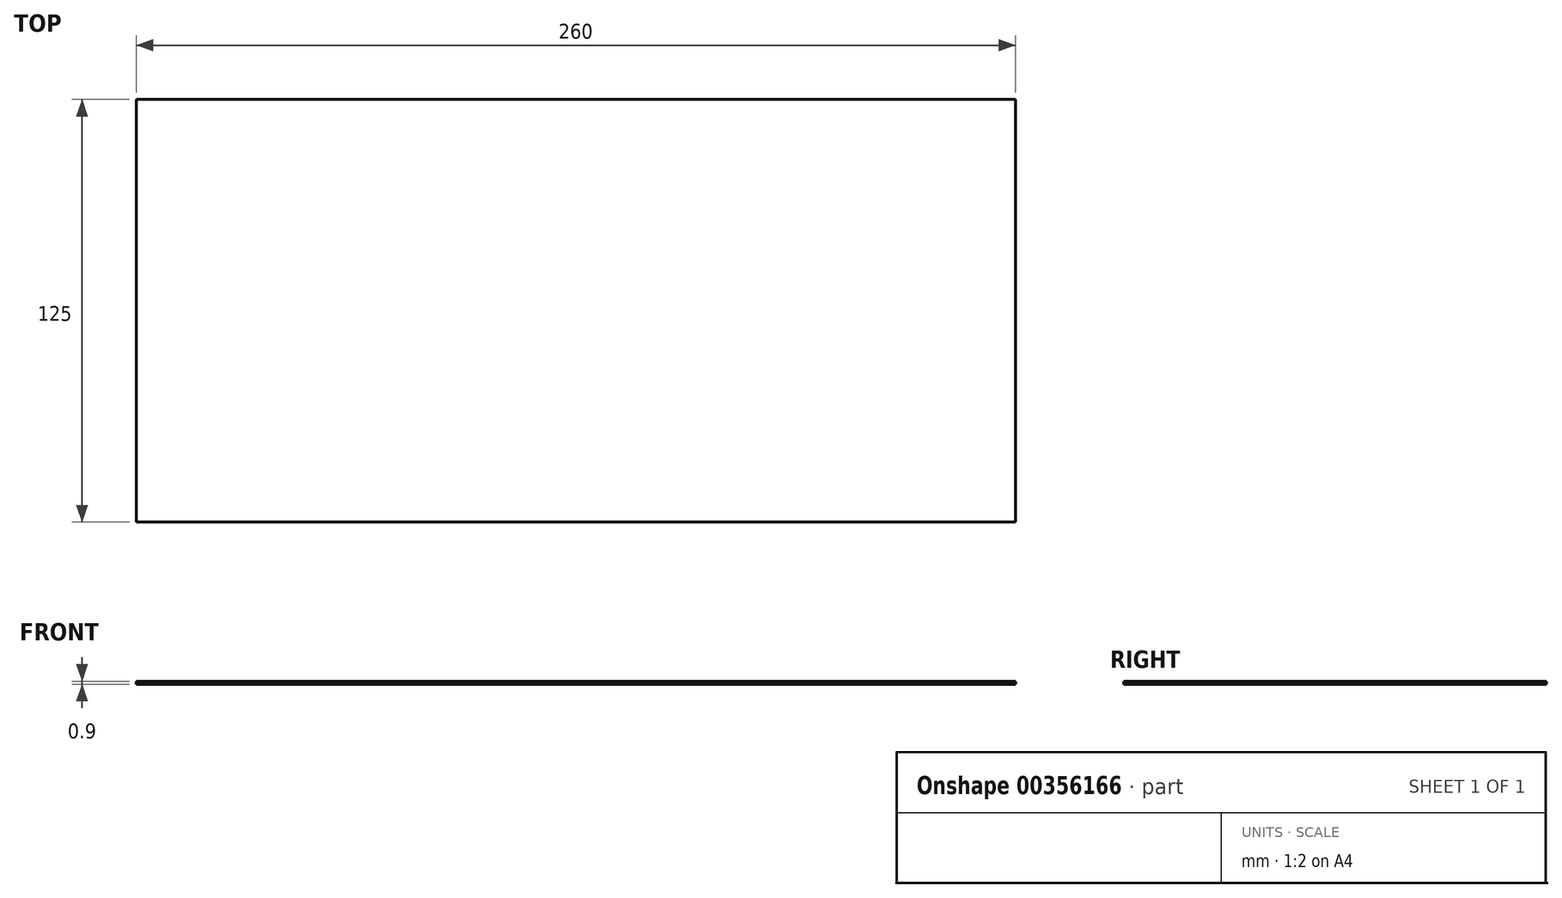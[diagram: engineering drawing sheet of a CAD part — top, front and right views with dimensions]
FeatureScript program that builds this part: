
annotation { "Feature Type Name" : "Feature", "Feature Type Description" : "" }
export const myFeature = defineFeature(function(context is Context, id is Id, definition is map)
    precondition{}
    {
        {
            var Q0;
            Q0=qCreatedBy(makeId("Top.planeOp"),FACE);
            var sketch = newSketch(context, id + "F0", { "sketchPlane" : qUnion([Q0])});
            skLineSegment(sketch, "E0.bottom", {"start": v(130, -62.5) * mm, "end": v(-130, -62.5) * mm});
            skLineSegment(sketch, "E0.top", {"start": v(130, 62.5) * mm, "end": v(-130, 62.5) * mm});
            skLineSegment(sketch, "E0.left", {"start": v(130, -62.5) * mm, "end": v(130, 62.5) * mm});
            skLineSegment(sketch, "E0.right", {"start": v(-130, -62.5) * mm, "end": v(-130, 62.5) * mm});
            skPoint(sketch, "E0.middle", {"position": v(0, 0) * mm});
            skSolve(sketch);
        }
        {
            var Q0;
            Q0 = qSketchRegion(id + "F0", true);
            extrude(context, id + "F1", {"entities" : qUnion([Q0]), "endBound" : BoundingType.SYMMETRIC, "depth" : 0.9 * mm});
        }
    });
